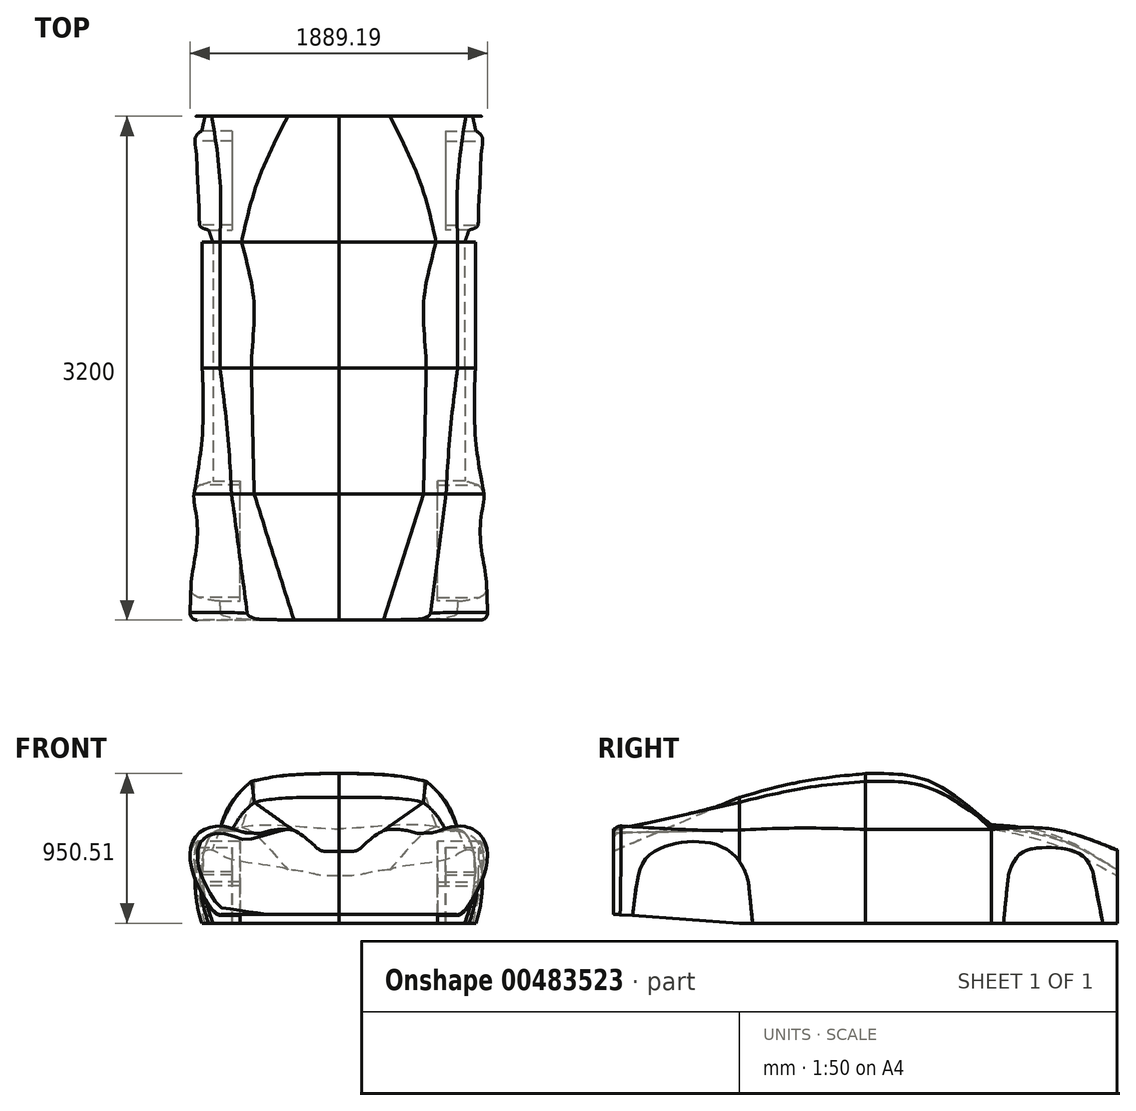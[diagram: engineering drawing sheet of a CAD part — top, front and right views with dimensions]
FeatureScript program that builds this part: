
annotation { "Feature Type Name" : "Feature", "Feature Type Description" : "" }
export const myFeature = defineFeature(function(context is Context, id is Id, definition is map)
    precondition{}
    {
        {
            var Q0;
            Q0=qCreatedBy(makeId("Front.planeOp"),FACE);
            cPlane(context, id + "F0", {"entities" : qUnion([Q0]), "cplaneType" : CPlaneType.OFFSET, "offset" : 400 * mm, "width" : 150 * mm, "height" : 150 * mm});
        }
        {
            var Q0;
            Q0=qCreatedBy(makeId("Front.planeOp"),FACE);
            cPlane(context, id + "F1", {"entities" : qUnion([Q0]), "cplaneType" : CPlaneType.OFFSET, "offset" : 400 * mm, "oppositeDirection" : true, "width" : 150 * mm, "height" : 150 * mm});
        }
        {
            var Q0;
            Q0=qCreatedBy(makeId("Front.planeOp"),FACE);
            cPlane(context, id + "F2", {"entities" : qUnion([Q0]), "cplaneType" : CPlaneType.OFFSET, "offset" : 800 * mm, "width" : 150 * mm, "height" : 150 * mm});
        }
        {
            var Q0;
            Q0=qCreatedBy(makeId("Front.planeOp"),FACE);
            cPlane(context, id + "F3", {"entities" : qUnion([Q0]), "cplaneType" : CPlaneType.OFFSET, "offset" : 800 * mm, "oppositeDirection" : true, "width" : 150 * mm, "height" : 150 * mm});
        }
        {
            var Q0;
            Q0=qCreatedBy(id+"F0.planeOp",FACE);
            var sketch = newSketch(context, id + "F4", { "sketchPlane" : qUnion([Q0])});
            skLineSegment(sketch, "E0", {"start": v(-437.64, -496.9) * mm, "end": v(362.36, -496.9) * mm});
            skFitSpline(sketch, "E1", {"points": [v(362.36, -496.9) * mm, v(411.37, -327.13) * mm, v(422.88, -64.41) * mm, v(362.36, 76.76) * mm, v(270.06, 107.64) * mm], "startDerivative": vector(197.67, 576.3) * mm, "endDerivative": vector(-315.03, 85.02) * mm});
            skFitSpline(sketch, "E2", {"points": [v(270.06, 107.64) * mm, v(225.54, 239.87) * mm, v(109.57, 359.67) * mm], "startDerivative": vector(-109.37, 364.31) * mm, "endDerivative": vector(-342.1, 275.59) * mm});
            skFitSpline(sketch, "E3", {"points": [v(109.57, 359.67) * mm, v(-93.9, 390.36) * mm, v(-437.64, 403.1) * mm], "startDerivative": vector(-435.27, 96.35) * mm, "endDerivative": vector(-663.86, -5.68) * mm});
            skLineSegment(sketch, "E4", {"start": v(-437.64, 403.1) * mm, "end": v(-437.64, -496.9) * mm});
            skSolve(sketch);
        }
        {
            var Q0;
            Q0=qCreatedBy(id+"F1.planeOp",FACE);
            var sketch = newSketch(context, id + "F5", { "sketchPlane" : qUnion([Q0])});
            skLineSegment(sketch, "E5", {"start": v(-437.64, -496.9) * mm, "end": v(362.36, -496.9) * mm});
            skFitSpline(sketch, "E6", {"points": [v(362.36, -496.9) * mm, v(411.37, -327.13) * mm, v(422.88, -64.41) * mm, v(362.36, 76.76) * mm, v(317.34, 98.7) * mm], "startDerivative": vector(197.67, 576.3) * mm, "endDerivative": vector(-315.03, 85.02) * mm});
            skFitSpline(sketch, "E7", {"points": [v(317.34, 98.7) * mm, v(233.9, 275.42) * mm, v(100.5, 364.64) * mm], "startDerivative": vector(-109.37, 364.31) * mm, "endDerivative": vector(-280.97, 134.3) * mm});
            skFitSpline(sketch, "E8", {"points": [v(100.5, 364.64) * mm, v(-101.44, 403.66) * mm, v(-437.64, 403.1) * mm], "startDerivative": vector(-435.27, 96.35) * mm, "endDerivative": vector(-663.86, -5.68) * mm});
            skLineSegment(sketch, "E9", {"start": v(-437.64, 403.1) * mm, "end": v(-437.64, -496.9) * mm});
            skSolve(sketch);
        }
        {
            var Q0;
            Q0=qCreatedBy(id+"F2.planeOp",FACE);
            var sketch = newSketch(context, id + "F6", { "sketchPlane" : qUnion([Q0])});
            skLineSegment(sketch, "E10", {"start": v(-437.64, -496.9) * mm, "end": v(362.36, -496.9) * mm});
            skFitSpline(sketch, "E11", {"points": [v(362.36, -496.9) * mm, v(420.32, -324.13) * mm, v(480.13, -55.27) * mm, v(362.36, 76.76) * mm, v(243.3, 95.74) * mm], "startDerivative": vector(197.67, 576.3) * mm, "endDerivative": vector(-315.03, 85.02) * mm});
            skFitSpline(sketch, "E12", {"points": [v(243.3, 95.74) * mm, v(189.7, 179.8) * mm, v(99.56, 271.16) * mm], "startDerivative": vector(-183.13, 286.64) * mm, "endDerivative": vector(-358.02, 310.73) * mm});
            skFitSpline(sketch, "E13", {"points": [v(99.56, 271.16) * mm, v(-96.57, 297.96) * mm, v(-437.64, 303.1) * mm], "startDerivative": vector(-435.27, 96.35) * mm, "endDerivative": vector(-663.86, -5.68) * mm});
            skLineSegment(sketch, "E14", {"start": v(-437.64, 303.1) * mm, "end": v(-437.64, -496.9) * mm});
            skSolve(sketch);
        }
        {
            var Q0;
            Q0=qCreatedBy(id+"F3.planeOp",FACE);
            var sketch = newSketch(context, id + "F7", { "sketchPlane" : qUnion([Q0])});
            skLineSegment(sketch, "E15", {"start": v(-437.64, -496.9) * mm, "end": v(362.36, -496.9) * mm});
            skFitSpline(sketch, "E16", {"points": [v(362.36, -496.9) * mm, v(411.37, -327.13) * mm, v(422.88, -64.41) * mm, v(362.36, 76.76) * mm, v(317.34, 98.7) * mm], "startDerivative": vector(197.67, 576.3) * mm, "endDerivative": vector(-315.03, 85.02) * mm});
            skFitSpline(sketch, "E17", {"points": [v(317.34, 98.7) * mm, v(232.34, 105.48) * mm, v(181.18, 115.23) * mm], "startDerivative": vector(-270.17, 31.04) * mm, "endDerivative": vector(-172.21, 37.01) * mm});
            skFitSpline(sketch, "E18", {"points": [v(181.18, 115.23) * mm, v(-108.75, 123.76) * mm, v(-437.64, 103.1) * mm], "startDerivative": vector(-435.27, 96.35) * mm, "endDerivative": vector(-663.86, -5.68) * mm});
            skLineSegment(sketch, "E19", {"start": v(-437.64, 103.1) * mm, "end": v(-437.64, -496.9) * mm});
            skSolve(sketch);
        }
        {
            var Q0;
            Q0=qCreatedBy(makeId("Front.planeOp"),FACE);
            var sketch = newSketch(context, id + "F8", { "sketchPlane" : qUnion([Q0])});
            skLineSegment(sketch, "E20", {"start": v(-437.64, -496.9) * mm, "end": v(362.36, -496.9) * mm});
            skFitSpline(sketch, "E21", {"points": [v(362.36, -496.9) * mm, v(411.37, -327.13) * mm, v(422.88, -64.41) * mm, v(362.36, 76.76) * mm, v(317.34, 98.7) * mm], "startDerivative": vector(197.67, 576.3) * mm, "endDerivative": vector(-315.03, 85.02) * mm});
            skFitSpline(sketch, "E22", {"points": [v(317.34, 98.7) * mm, v(233.9, 275.42) * mm, v(116.98, 404.65) * mm], "startDerivative": vector(-109.37, 364.31) * mm, "endDerivative": vector(-342.1, 275.59) * mm});
            skFitSpline(sketch, "E23", {"points": [v(116.98, 404.65) * mm, v(-86.1, 440.04) * mm, v(-437.64, 453.1) * mm], "startDerivative": vector(-435.27, 96.35) * mm, "endDerivative": vector(-663.86, -5.68) * mm});
            skLineSegment(sketch, "E24", {"start": v(-437.64, 453.1) * mm, "end": v(-437.64, -496.9) * mm});
            skSolve(sketch);
        }
        {
            var Q0;
            Q0=makeQuery(id+"F8.imprint","IMPRINT",FACE,{"disambiguationData":[TD([[makeQuery(id+"F8.imprint","IMPRINT",EDGE,{"derivedFrom":sQuery(id+"F8.wireOp",EDGE,"E20")}),1.0]])]});
            var Q1;
            Q1=makeQuery(id+"F4.imprint","IMPRINT",FACE,{"disambiguationData":[TD([[makeQuery(id+"F4.imprint","IMPRINT",EDGE,{"derivedFrom":sQuery(id+"F4.wireOp",EDGE,"E0")}),1.0]])]});
            var Q2;
            Q2=makeQuery(id+"F6.imprint","IMPRINT",FACE,{"disambiguationData":[TD([[makeQuery(id+"F6.imprint","IMPRINT",EDGE,{"derivedFrom":sQuery(id+"F6.wireOp",EDGE,"E10")}),1.0]])]});
            loft(context, id + "F9", {"sheetProfilesArray" : [{ "sheetProfileEntities" : qUnion([Q0]) }, { "sheetProfileEntities" : qUnion([Q1]) }, { "sheetProfileEntities" : qUnion([Q2]) }]});
        }
        {
            var Q1;
            Q1=makeQuery(id+"F9.opLoft","CAP_FACE",FACE,{"disambiguationData":[OSD([makeQuery(id+"F8.imprint","IMPRINT",FACE,{"disambiguationData":[TD([[makeQuery(id+"F8.imprint","IMPRINT",EDGE,{"derivedFrom":sQuery(id+"F8.wireOp",EDGE,"E20")}),1.0]])]})])],"isStart":true});
            var Q2;
            Q2=makeQuery(id+"F5.imprint","IMPRINT",FACE,{"disambiguationData":[TD([[makeQuery(id+"F5.imprint","IMPRINT",EDGE,{"derivedFrom":sQuery(id+"F5.wireOp",EDGE,"E5")}),1.0]])]});
            var Q3;
            Q3=makeQuery(id+"F7.imprint","IMPRINT",FACE,{"disambiguationData":[TD([[makeQuery(id+"F7.imprint","IMPRINT",EDGE,{"derivedFrom":sQuery(id+"F7.wireOp",EDGE,"E15")}),1.0]])]});
            loft(context, id + "F10", {"operationType" : NewBodyOperationType.ADD, "startCondition" : LoftEndDerivativeType.NORMAL_TO_PROFILE, "startMagnitude" : 1, "sheetProfilesArray" : [{ "sheetProfileEntities" : qUnion([Q1]) }, { "sheetProfileEntities" : qUnion([Q2]) }, { "sheetProfileEntities" : qUnion([Q3]) }]});
        }
        {
            var Q0;
            Q0=qCreatedBy(makeId("Front.planeOp"),FACE);
            cPlane(context, id + "F11", {"entities" : qUnion([Q0]), "cplaneType" : CPlaneType.OFFSET, "offset" : 1600 * mm, "width" : 150 * mm, "height" : 150 * mm});
        }
        {
            var Q0;
            Q0=qCreatedBy(id+"F11.planeOp",FACE);
            var sketch = newSketch(context, id + "F12", { "sketchPlane" : qUnion([Q0])});
            skLineSegment(sketch, "E25", {"start": v(-437.63, -439.78) * mm, "end": v(312.37, -439.78) * mm});
            skFitSpline(sketch, "E26", {"points": [v(312.37, -439.78) * mm, v(406.35, -349.14) * mm, v(497.07, -149) * mm, v(483.17, 39.36) * mm, v(312.37, 122.45) * mm, v(138.6, 77.16) * mm], "startDerivative": vector(612.1, 63.77) * mm, "endDerivative": vector(-315.03, 85.02) * mm});
            skFitSpline(sketch, "E27", {"points": [v(138.6, 77.16) * mm, v(29.83, 81.91) * mm, v(-152.39, 91.62) * mm], "startDerivative": vector(-631.39, -51.17) * mm, "endDerivative": vector(-287.8, -108.16) * mm});
            skFitSpline(sketch, "E28", {"points": [v(-152.39, 91.62) * mm, v(-303.77, -23.15) * mm, v(-437.63, -39.78) * mm], "startDerivative": vector(-333.07, -142) * mm, "endDerivative": vector(-663.86, -5.68) * mm});
            skLineSegment(sketch, "E29", {"start": v(-437.63, -39.78) * mm, "end": v(-437.63, -439.78) * mm});
            skSolve(sketch);
        }
        {
            var Q1;
            Q1=qSketchRegion(id+"F12",true);
            var Q2;
            Q2=qSketchRegion(id+"F6",true);
            loft(context, id + "F13", {"operationType" : NewBodyOperationType.ADD, "sheetProfilesArray" : [{ "sheetProfileEntities" : qUnion([Q1]) }, { "sheetProfileEntities" : qUnion([Q2]) }]});
        }
        {
            var Q0;
            Q0=qCreatedBy(makeId("Right.planeOp"),FACE);
            cPlane(context, id + "F14", {"entities" : qUnion([Q0]), "cplaneType" : CPlaneType.OFFSET, "offset" : 800 * mm, "width" : 150 * mm, "height" : 150 * mm});
        }
        {
            var Q0;
            Q0=qCreatedBy(id+"F14.planeOp",FACE);
            var sketch = newSketch(context, id + "F15", { "sketchPlane" : qUnion([Q0])});
            skLineSegment(sketch, "E30", {"start": v(-743.36, -235.3) * mm, "end": v(-696.56, -680.73) * mm});
            skLineSegment(sketch, "E31", {"start": v(-696.56, -680.73) * mm, "end": v(-1508.45, -680.73) * mm});
            skLineSegment(sketch, "E32", {"start": v(-1508.45, -680.73) * mm, "end": v(-1455.6, -258.17) * mm});
            skFitSpline(sketch, "E33", {"points": [v(-1455.6, -258.17) * mm, v(-1367.73, -59.54) * mm, v(-939.89, 0) * mm, v(-743.36, -235.3) * mm], "startDerivative": vector(179.38, 766.9) * mm, "endDerivative": vector(215.74, -934.6) * mm});
            skSolve(sketch);
        }
        {
            var Q0;
            Q0=makeQuery(id+"F15.imprint","IMPRINT",FACE,{"disambiguationData":[TD([[makeQuery(id+"F15.imprint","IMPRINT",EDGE,{"derivedFrom":sQuery(id+"F15.wireOp",EDGE,"E30")}),-1.0]])]});
            extrude(context, id + "F16", {"entities" : qUnion([Q0]), "operationType" : NewBodyOperationType.REMOVE, "oppositeDirection" : true, "depth" : 610 * mm});
        }
        {
            var Q0;
            Q0=qCreatedBy(makeId("Front.planeOp"),FACE);
            cPlane(context, id + "F17", {"entities" : qUnion([Q0]), "cplaneType" : CPlaneType.OFFSET, "offset" : 1600 * mm, "oppositeDirection" : true, "width" : 150 * mm, "height" : 150 * mm});
        }
        {
            var Q0;
            Q0=qCreatedBy(id+"F17.planeOp",FACE);
            var sketch = newSketch(context, id + "F18", { "sketchPlane" : qUnion([Q0])});
            skLineSegment(sketch, "E34", {"start": v(-437.64, -496.9) * mm, "end": v(412.36, -496.9) * mm});
            skFitSpline(sketch, "E35", {"points": [v(412.36, -496.9) * mm, v(453.24, -312.76) * mm, v(468.47, -212.95) * mm, v(458.13, -104.07) * mm, v(368.95, -34.17) * mm], "startDerivative": vector(197.67, 576.3) * mm, "endDerivative": vector(-632.8, -161.78) * mm});
            skFitSpline(sketch, "E36", {"points": [v(368.95, -34.17) * mm, v(263.14, -86.74) * mm, v(-113.63, -157.63) * mm], "startDerivative": vector(-380.63, -87.62) * mm, "endDerivative": vector(-231.79, -133.75) * mm});
            skFitSpline(sketch, "E37", {"points": [v(-113.63, -157.63) * mm, v(-279.1, -183.63) * mm, v(-437.64, -196.9) * mm], "startDerivative": vector(-388.75, -15.86) * mm, "endDerivative": vector(-663.86, -5.68) * mm});
            skLineSegment(sketch, "E38", {"start": v(-437.64, -196.9) * mm, "end": v(-437.64, -496.9) * mm});
            skSolve(sketch);
        }
        {
            var Q0;
            Q0=qCreatedBy(id+"F17.planeOp",FACE);
            cPlane(context, id + "F19", {"entities" : qUnion([Q0]), "cplaneType" : CPlaneType.OFFSET, "offset" : 400 * mm, "width" : 150 * mm, "height" : 150 * mm});
        }
        {
            var Q0;
            Q0=qCreatedBy(id+"F19.planeOp",FACE);
            var sketch = newSketch(context, id + "F20", { "sketchPlane" : qUnion([Q0])});
            skLineSegment(sketch, "E39", {"start": v(-437.64, -496.9) * mm, "end": v(462.36, -496.9) * mm});
            skFitSpline(sketch, "E40", {"points": [v(462.36, -496.9) * mm, v(486.38, -325.83) * mm, v(475.5, -116.9) * mm, v(421.85, 53.8) * mm, v(317.34, 98.7) * mm], "startDerivative": vector(197.67, 576.3) * mm, "endDerivative": vector(-315.03, 85.02) * mm});
            skFitSpline(sketch, "E41", {"points": [v(317.34, 98.7) * mm, v(168.52, 51.04) * mm, v(72.04, 48.95) * mm], "startDerivative": vector(-360.94, 2.04) * mm, "endDerivative": vector(-390.07, 72.23) * mm});
            skFitSpline(sketch, "E42", {"points": [v(72.04, 48.95) * mm, v(-127.4, 56.45) * mm, v(-437.64, 3.1) * mm], "startDerivative": vector(-435.27, 96.35) * mm, "endDerivative": vector(-663.86, -5.68) * mm});
            skLineSegment(sketch, "E43", {"start": v(-437.64, 3.1) * mm, "end": v(-437.64, -496.9) * mm});
            skSolve(sketch);
        }
        {
            var Q1;
            Q1=makeQuery(id+"F10.opLoft","CAP_FACE",FACE,{"disambiguationData":[OSD([makeQuery(id+"F7.imprint","IMPRINT",FACE,{"disambiguationData":[TD([[makeQuery(id+"F7.imprint","IMPRINT",EDGE,{"derivedFrom":sQuery(id+"F7.wireOp",EDGE,"E15")}),1.0]])]})])],"isStart":true});
            var Q2;
            Q2=makeQuery(id+"F20.imprint","IMPRINT",FACE,{"disambiguationData":[TD([[makeQuery(id+"F20.imprint","IMPRINT",EDGE,{"derivedFrom":sQuery(id+"F20.wireOp",EDGE,"E39")}),1.0]])]});
            var Q3;
            Q3=makeQuery(id+"F18.imprint","IMPRINT",FACE,{"disambiguationData":[TD([[makeQuery(id+"F18.imprint","IMPRINT",EDGE,{"derivedFrom":sQuery(id+"F18.wireOp",EDGE,"E34")}),1.0]])]});
            loft(context, id + "F21", {"operationType" : NewBodyOperationType.ADD, "sheetProfilesArray" : [{ "sheetProfileEntities" : qUnion([Q1]) }, { "sheetProfileEntities" : qUnion([Q2]) }, { "sheetProfileEntities" : qUnion([Q3]) }]});
        }
        {
            var Q0;
            Q0=qCreatedBy(id+"F14.planeOp",FACE);
            var sketch = newSketch(context, id + "F22", { "sketchPlane" : qUnion([Q0])});
            skLineSegment(sketch, "E44", {"start": v(908.1, -190.95) * mm, "end": v(867.24, -590.52) * mm});
            skLineSegment(sketch, "E45", {"start": v(867.24, -590.52) * mm, "end": v(1525.62, -590.52) * mm});
            skLineSegment(sketch, "E46", {"start": v(1525.62, -590.52) * mm, "end": v(1443.9, -170.52) * mm});
            skFitSpline(sketch, "E47", {"points": [v(1443.9, -170.52) * mm, v(1357.62, -54.74) * mm, v(1166.92, -16.14) * mm, v(987.57, -54.74) * mm, v(908.1, -190.95) * mm], "startDerivative": vector(-221.05, 690.8) * mm, "endDerivative": vector(-187.84, -657.45) * mm});
            skSolve(sketch);
        }
        {
            var Q0;
            Q0=makeQuery(id+"F22.imprint","IMPRINT",FACE,{"disambiguationData":[TD([[makeQuery(id+"F22.imprint","IMPRINT",EDGE,{"derivedFrom":sQuery(id+"F22.wireOp",EDGE,"E44")}),1.0]])]});
            extrude(context, id + "F23", {"entities" : qUnion([Q0]), "operationType" : NewBodyOperationType.REMOVE, "oppositeDirection" : true, "depth" : 561 * mm});
        }
        {
            var Q0;
            {var subQ0=sQuery(id+"F8.wireOp",EDGE,"E24");var subQ1=sQuery(id+"F8.wireOp",EDGE,"E21");var subQ2=sQuery(id+"F8.wireOp",EDGE,"E20");Q0=makeQuery(id+"F21.boolean.opBoolean","MERGE",FACE,{"derivedFrom":[makeQuery(id+"F13.boolean.opBoolean","MERGE",FACE,{"derivedFrom":[makeQuery(id+"F10.boolean.opBoolean","MERGE",FACE,{"derivedFrom":[makeQuery(id+"F9.opLoft","SWEPT_FACE",FACE,{"disambiguationData":[OSD([sQuery(id+"F4.wireOp",EDGE,"E0"),sQuery(id+"F4.wireOp",EDGE,"E1"),sQuery(id+"F4.wireOp",EDGE,"E4"),subQ2,subQ1,subQ0])]}),makeQuery(id+"F10.opLoft","SWEPT_FACE",FACE,{"disambiguationData":[OSD([sQuery(id+"F5.wireOp",EDGE,"E5"),sQuery(id+"F5.wireOp",EDGE,"E6"),sQuery(id+"F5.wireOp",EDGE,"E9"),subQ2,subQ1,subQ0])]})]}),makeQuery(id+"F13.opLoft","SWEPT_FACE",FACE,{"disambiguationData":[OSD([sQuery(id+"F6.wireOp",EDGE,"E10"),sQuery(id+"F6.wireOp",EDGE,"E11"),sQuery(id+"F6.wireOp",EDGE,"E14"),sQuery(id+"F12.wireOp",EDGE,"E25"),sQuery(id+"F12.wireOp",EDGE,"E26"),sQuery(id+"F12.wireOp",EDGE,"E29")])]})]}),makeQuery(id+"F21.opLoft","SWEPT_FACE",FACE,{"disambiguationData":[OSD([sQuery(id+"F7.wireOp",EDGE,"E15"),sQuery(id+"F7.wireOp",EDGE,"E16"),sQuery(id+"F7.wireOp",EDGE,"E19"),sQuery(id+"F20.wireOp",EDGE,"E39"),sQuery(id+"F20.wireOp",EDGE,"E40"),sQuery(id+"F20.wireOp",EDGE,"E43")])]})]});}
            var sketch = newSketch(context, id + "F24", { "sketchPlane" : qUnion([Q0])});
            skFitSpline(sketch, "E48", {"points": [v(412.36, -1600) * mm, v(366.73, -1888.42) * mm, v(211.75, -2042.28) * mm, v(-139.29, -2091.57) * mm, v(-438.85, -2086.37) * mm], "startDerivative": vector(-69.7, -1240.37) * mm, "endDerivative": vector(-1120.26, 39.16) * mm});
            skLineSegment(sketch, "E49", {"start": v(-438.85, -2086.37) * mm, "end": v(-437.64, -1600) * mm});
            skLineSegment(sketch, "E50", {"start": v(-437.64, -1600) * mm, "end": v(412.36, -1600) * mm});
            skSolve(sketch);
        }
        {
            var Q0;
            Q0=makeQuery(id+"F9.opLoft","SWEPT_BODY",BODY,{"disambiguationData":[OSD([sQuery(id+"F4.wireOp",EDGE,"E2"),makeQuery(id+"F6.imprint","IMPRINT",FACE,{"disambiguationData":[TD([[makeQuery(id+"F6.imprint","IMPRINT",EDGE,{"derivedFrom":sQuery(id+"F6.wireOp",EDGE,"E10")}),1.0]])]}),makeQuery(id+"F8.imprint","IMPRINT",FACE,{"disambiguationData":[TD([[makeQuery(id+"F8.imprint","IMPRINT",EDGE,{"derivedFrom":sQuery(id+"F8.wireOp",EDGE,"E20")}),1.0]])]})])]});
            var Q1;
            {var subQ0=sQuery(id+"F8.wireOp",EDGE,"E24");var subQ1=sQuery(id+"F8.wireOp",EDGE,"E23");var subQ2=sQuery(id+"F8.wireOp",EDGE,"E20");Q1=makeQuery(id+"F21.boolean.opBoolean","MERGE",FACE,{"derivedFrom":[makeQuery(id+"F13.boolean.opBoolean","MERGE",FACE,{"derivedFrom":[makeQuery(id+"F10.boolean.opBoolean","MERGE",FACE,{"derivedFrom":[makeQuery(id+"F9.opLoft","SWEPT_FACE",FACE,{"disambiguationData":[OSD([sQuery(id+"F4.wireOp",EDGE,"E0"),sQuery(id+"F4.wireOp",EDGE,"E3"),sQuery(id+"F4.wireOp",EDGE,"E4"),subQ2,subQ1,subQ0])]}),makeQuery(id+"F10.opLoft","SWEPT_FACE",FACE,{"disambiguationData":[OSD([sQuery(id+"F5.wireOp",EDGE,"E5"),sQuery(id+"F5.wireOp",EDGE,"E8"),sQuery(id+"F5.wireOp",EDGE,"E9"),subQ2,subQ1,subQ0])]})]}),makeQuery(id+"F13.opLoft","SWEPT_FACE",FACE,{"disambiguationData":[OSD([sQuery(id+"F6.wireOp",EDGE,"E10"),sQuery(id+"F6.wireOp",EDGE,"E13"),sQuery(id+"F6.wireOp",EDGE,"E14"),sQuery(id+"F12.wireOp",EDGE,"E25"),sQuery(id+"F12.wireOp",EDGE,"E28"),sQuery(id+"F12.wireOp",EDGE,"E29")])]})]}),makeQuery(id+"F21.opLoft","SWEPT_FACE",FACE,{"disambiguationData":[OSD([sQuery(id+"F7.wireOp",EDGE,"E15"),sQuery(id+"F7.wireOp",EDGE,"E18"),sQuery(id+"F7.wireOp",EDGE,"E19"),sQuery(id+"F20.wireOp",EDGE,"E39"),sQuery(id+"F20.wireOp",EDGE,"E42"),sQuery(id+"F20.wireOp",EDGE,"E43")])]})]});}
            mirror(context, id + "F25", {"operationType" : NewBodyOperationType.ADD, "entities" : qUnion([Q0]), "mirrorPlane" : qUnion([Q1])});
        }
        {
            var Q0;
            Q0=makeQuery(id+"F24.imprint","IMPRINT",FACE,{"disambiguationData":[TD([[makeQuery(id+"F24.imprint","IMPRINT",EDGE,{"derivedFrom":sQuery(id+"F24.wireOp",EDGE,"E48")}),-1.0]])]});
            var sketch = newSketch(context, id + "F26", { "sketchPlane" : qUnion([Q0])});
            skSolve(sketch);
        }
        {
            var Q0;
            Q0=makeQuery(id+"F13.opLoft","MID_CAP_EDGE",EDGE,{"disambiguationData":[OSD([sQuery(id+"F12.wireOp",EDGE,"E25"),sQuery(id+"F12.wireOp",EDGE,"E26"),sQuery(id+"F12.wireOp",EDGE,"E27")])],"capPos":0.0});
            fillet(context, id + "F27", {"entities" : qUnion([Q0]), "radius" : 45 * mm, "tangentPropagation" : true, "allowEdgeOverflow" : false});
        }
        {
            var Q0;
            Q0=makeQuery(id+"F25.opPattern","COPY",EDGE,{"derivedFrom":makeQuery(id+"F13.opLoft","MID_CAP_EDGE",EDGE,{"disambiguationData":[OSD([sQuery(id+"F12.wireOp",EDGE,"E25"),sQuery(id+"F12.wireOp",EDGE,"E26"),sQuery(id+"F12.wireOp",EDGE,"E27")])],"capPos":0.0}),"instanceName":"1"});
            fillet(context, id + "F28", {"entities" : qUnion([Q0]), "radius" : 45 * mm, "tangentPropagation" : true, "allowEdgeOverflow" : false});
        }
    });
